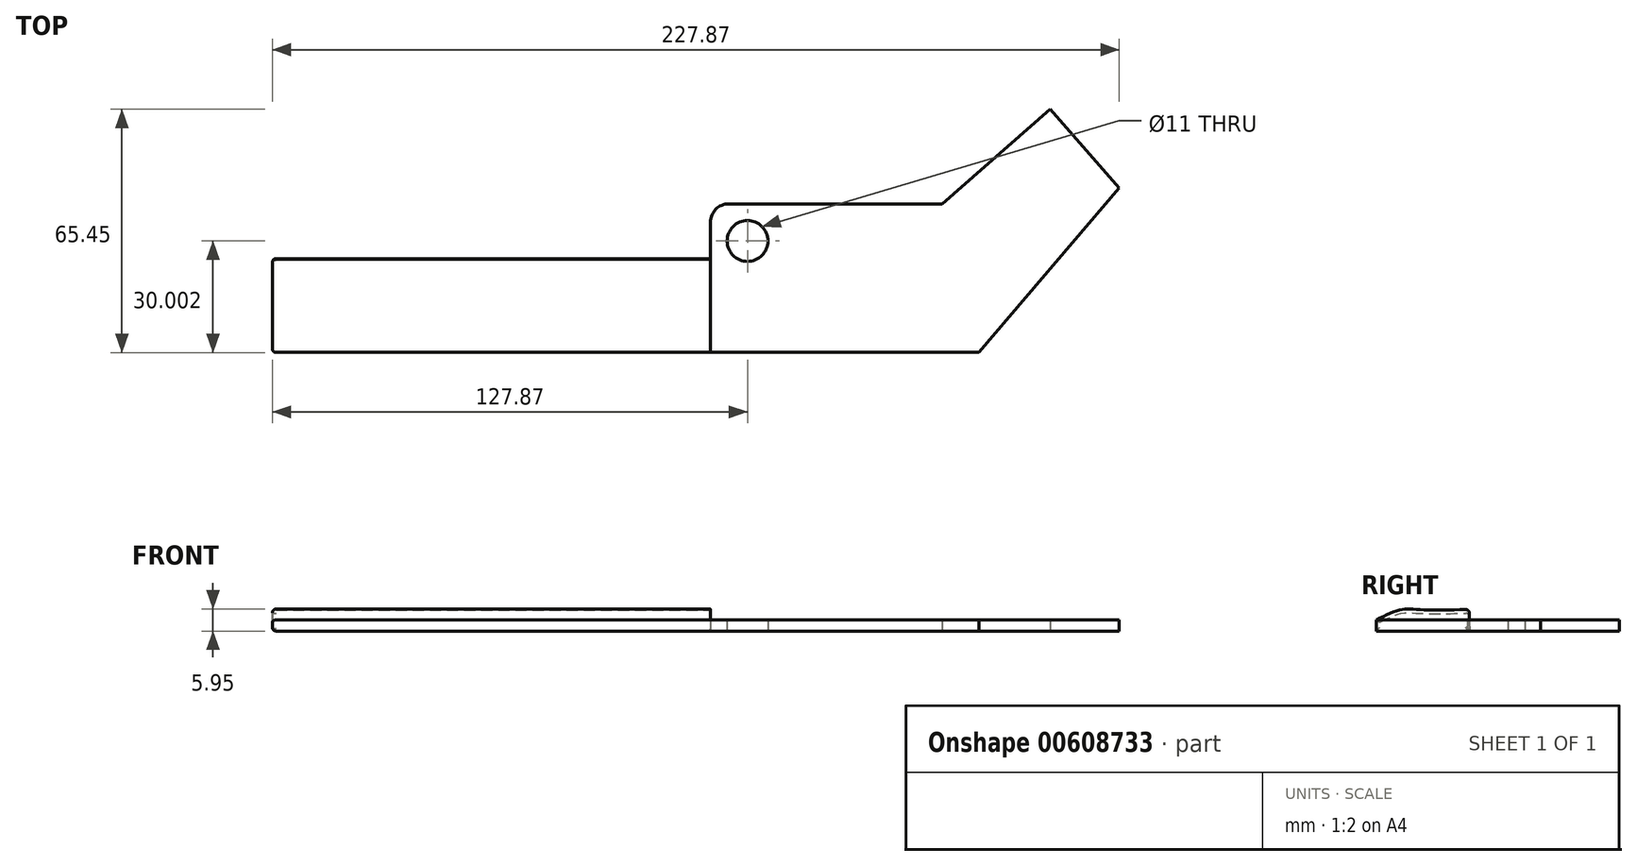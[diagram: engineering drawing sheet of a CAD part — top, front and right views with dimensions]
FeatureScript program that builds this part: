
annotation { "Feature Type Name" : "Feature", "Feature Type Description" : "" }
export const myFeature = defineFeature(function(context is Context, id is Id, definition is map)
    precondition{}
    {
        {
            var Q0;
            Q0=qCreatedBy(makeId("Top.planeOp"),FACE);
            var sketch = newSketch(context, id + "F0", { "sketchPlane" : qUnion([Q0])});
            skLineSegment(sketch, "E0", {"start": v(110, 33.11) * mm, "end": v(91.4, 54.3) * mm});
            skLineSegment(sketch, "E1", {"start": v(91.4, 54.3) * mm, "end": v(62.43, 28.85) * mm});
            skLineSegment(sketch, "E2", {"start": v(62.43, 28.85) * mm, "end": v(0, 28.85) * mm});
            skLineSegment(sketch, "E3", {"start": v(0, 28.85) * mm, "end": v(0, 13.85) * mm});
            skLineSegment(sketch, "E4", {"start": v(0, 13.85) * mm, "end": v(-117.87, 13.85) * mm});
            skLineSegment(sketch, "E5", {"start": v(-117.87, 13.85) * mm, "end": v(-117.87, -11.15) * mm});
            skLineSegment(sketch, "E6", {"start": v(-117.87, -11.15) * mm, "end": v(72.3, -11.15) * mm});
            skLineSegment(sketch, "E7", {"start": v(72.3, -11.15) * mm, "end": v(110, 33.11) * mm});
            skPoint(sketch, "E8", {"position": v(10, 18.85) * mm});
            skSolve(sketch);
        }
        {
            var Q0;
            Q0=makeQuery(id+"F0.imprint","IMPRINT",FACE,{"disambiguationData":[TD([[makeQuery(id+"F0.imprint","IMPRINT",EDGE,{"derivedFrom":sQuery(id+"F0.wireOp",EDGE,"E0")}),1.0]])]});
            extrude(context, id + "F1", {"entities" : qUnion([Q0]), "depth" : 3 * mm, "offsetDistance" : 25 * mm});
        }
        {
            var Q0;
            Q0=sQuery(id+"F0.wireOp",VERTEX,"E8");
            var Q1;
            Q1=makeQuery(id+"F1.opExtrude","SWEPT_BODY",BODY,{"disambiguationData":[OSD([sQuery(id+"F0.wireOp",EDGE,"E0"),sQuery(id+"F0.wireOp",EDGE,"E1"),sQuery(id+"F0.wireOp",EDGE,"E2"),sQuery(id+"F0.wireOp",EDGE,"E3"),sQuery(id+"F0.wireOp",EDGE,"E4"),sQuery(id+"F0.wireOp",EDGE,"E5"),sQuery(id+"F0.wireOp",EDGE,"E6"),sQuery(id+"F0.wireOp",EDGE,"E7")])]});
            hole(context, id + "F2", {"style" : HoleStyle.SIMPLE, "endStyle" : HoleEndStyle.THROUGH, "oppositeDirection" : true, "standardTappedOrClearance" : lookupTablePath({ "fit" : "Normal", "standard" : "ISO", "size" : "M10", "type" : "Clearance" }), "standardBlindInLast" : lookupTablePath({ "fit" : "Standard", "standard" : "ISO", "size" : "M10", "type" : "Clearance" }), "holeDiameter" : 11 * mm, "majorDiameter" : 5 * mm, "isTappedThrough" : true, "tappedDepth" : 12 * mm, "tapClearance" : 3, "locations" : qUnion([Q0]), "scope" : qUnion([Q1])});
        }
        {
            var Q0;
            Q0=makeQuery(id+"F1.opExtrude","SWEPT_EDGE",EDGE,{"disambiguationData":[OSD([sQuery(id+"F0.wireOp",EDGE,"E2"),sQuery(id+"F0.wireOp",EDGE,"E3")])]});
            fillet(context, id + "F3", {"entities" : qUnion([Q0]), "radius" : 5 * mm, "tangentPropagation" : true, "allowEdgeOverflow" : false});
        }
        {
            var Q0;
            Q0=qCreatedBy(makeId("Right.planeOp"),FACE);
            var sketch = newSketch(context, id + "F4", { "sketchPlane" : qUnion([Q0])});
            skArc(sketch, "E9", {"start": v(13.97, 4.63) * mm, "mid": v(13.87, 2.3) * mm, "end": v(14.26, 0) * mm});
            skLineSegment(sketch, "E10.0", {"start": v(13.85, 3) * mm, "end": v(-11.15, 3) * mm});
            skLineSegment(sketch, "E10.1", {"start": v(-11.15, 3) * mm, "end": v(-11.15, 0) * mm});
            skFitSpline(sketch, "E11", {"points": [v(14.2, 5.8) * mm, v(0, 5.8) * mm, v(-4.46, 5.8) * mm, v(-11.15, 3) * mm], "startDerivative": vector(-37.6, -0.65) * mm, "endDerivative": vector(-23.03, -11.5) * mm});
            skArc(sketch, "E12.filletArc", {"start": v(13.97, 4.63) * mm, "mid": v(13.73, 5.43) * mm, "end": v(12.96, 5.77) * mm});
            skLineSegment(sketch, "E13", {"start": v(14.26, 0) * mm, "end": v(-11.15, 0) * mm});
            skSolve(sketch);
        }
        {
            var Q0;
            {var subQ2=sQuery(id+"F4.wireOp",EDGE,"E10.0");Q0=makeQuery(id+"F4.imprint","IMPRINT",FACE,{"disambiguationData":[TD([[makeQuery(id+"F4.imprint","IMPRINT",EDGE,{"derivedFrom":subQ2}),-1.0]])]});}
            var Q1;
            {var subQ2=sQuery(id+"F4.wireOp",EDGE,"E10.0");Q1=makeQuery(id+"F4.imprint","IMPRINT",FACE,{"disambiguationData":[TD([[makeQuery(id+"F4.imprint","IMPRINT",EDGE,{"derivedFrom":subQ2}),1.0]])]});}
            var Q2;
            Q2=makeQuery(id+"F1.opExtrude","SWEPT_FACE",FACE,{"disambiguationData":[OSD([sQuery(id+"F0.wireOp",EDGE,"E5")])]});
            extrude(context, id + "F5", {"entities" : qUnion([Q0, Q1]), "operationType" : NewBodyOperationType.ADD, "endBound" : BoundingType.UP_TO_SURFACE, "oppositeDirection" : true, "depth" : 25 * mm, "endBoundEntityFace" : qUnion([Q2]), "offsetDistance" : 25 * mm});
        }
        {
            var Q0;
            Q0=makeQuery(id+"F5.opExtrude","SWEPT_EDGE",EDGE,{"disambiguationData":[OSD([sQuery(id+"F4.wireOp",EDGE,"E9"),sQuery(id+"F4.wireOp",EDGE,"E13")])]});
            fillet(context, id + "F6", {"entities" : qUnion([Q0]), "radius" : .5 * mm, "tangentPropagation" : true, "allowEdgeOverflow" : false});
        }
        {
            var Q0;
            Q0=makeQuery(id+"F5.opExtrude","CAP_EDGE",EDGE,{"disambiguationData":[OSD([sQuery(id+"F4.wireOp",EDGE,"E9")])],"isStart":false});
            var Q1;
            Q1=makeQuery(id+"F1.opExtrude","SWEPT_EDGE",EDGE,{"disambiguationData":[OSD([sQuery(id+"F0.wireOp",EDGE,"E5"),sQuery(id+"F0.wireOp",EDGE,"E6")])]});
            fillet(context, id + "F7", {"entities" : qUnion([Q0, Q1]), "radius" : 1 * mm, "tangentPropagation" : true, "allowEdgeOverflow" : false});
        }
    });
